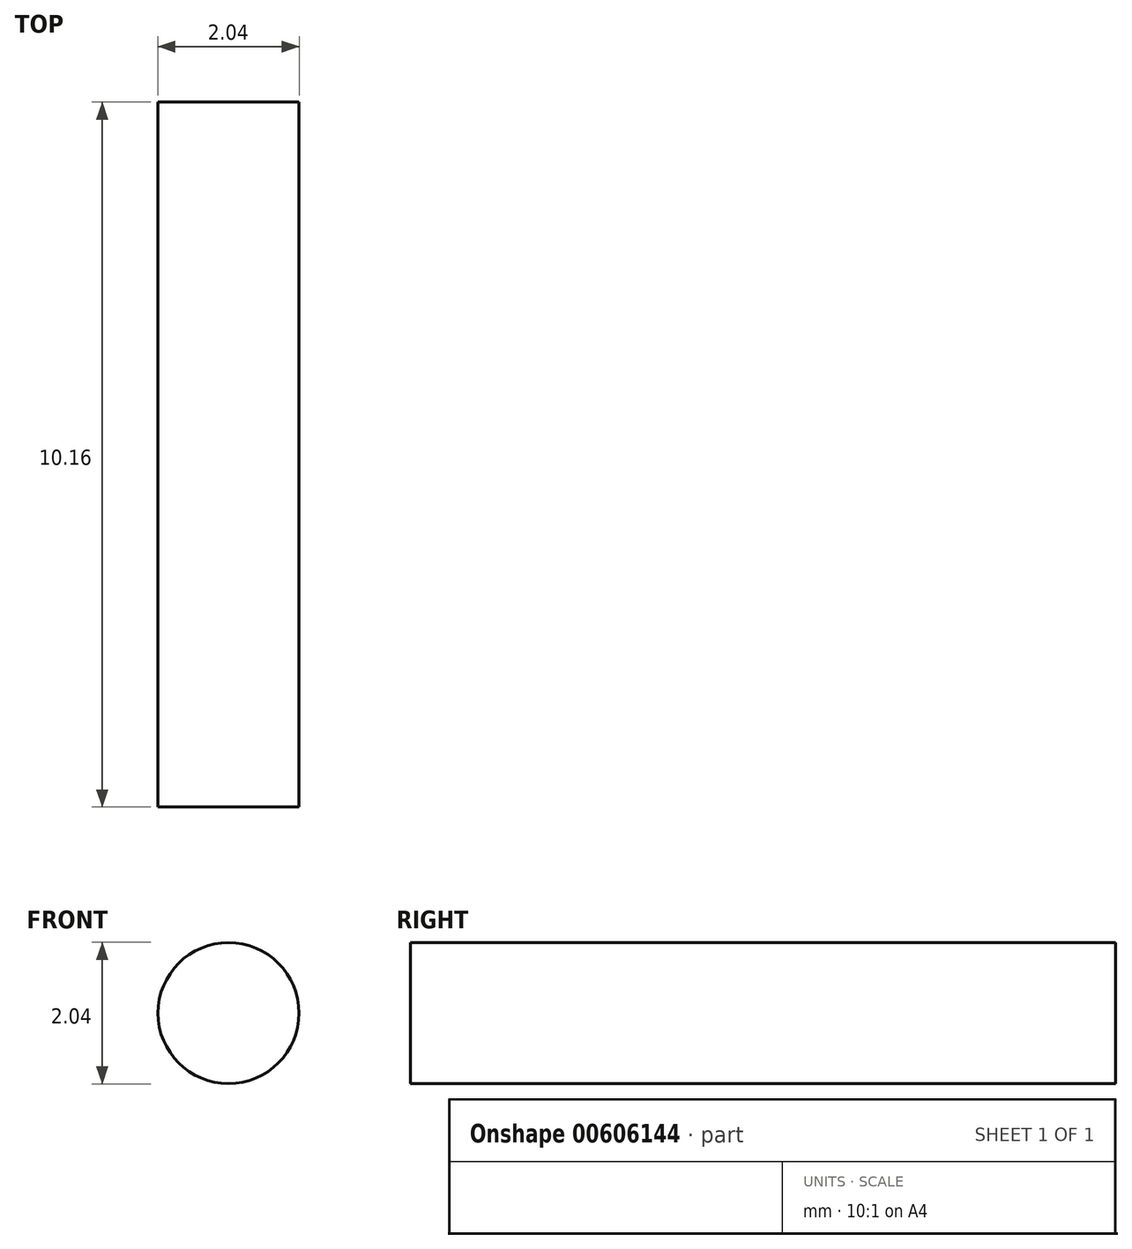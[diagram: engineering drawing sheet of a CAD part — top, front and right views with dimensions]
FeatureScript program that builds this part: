
annotation { "Feature Type Name" : "Feature", "Feature Type Description" : "" }
export const myFeature = defineFeature(function(context is Context, id is Id, definition is map)
    precondition{}
    {
        {
            var Q0;
            Q0=qCreatedBy(makeId("Front.planeOp"),FACE);
            var sketch = newSketch(context, id + "F0", { "sketchPlane" : qUnion([Q0])});
            skCircle(sketch, "E0", {"center": v(0, 0) * mm, "radius": 1.02 * mm});
            skSolve(sketch);
        }
        {
            var Q0;
            Q0 = qSketchRegion(id + "F0", true);
            var Q1;
            Q1=makeQuery(id+"F0.imprint","IMPRINT",FACE,{"disambiguationData":[TD([[makeQuery(id+"F0.imprint","IMPRINT",EDGE,{"derivedFrom":sQuery(id+"F0.wireOp",EDGE,"E0")}),1.0]])]});
            extrude(context, id + "F1", {"entities" : qUnion([Q0, Q1]), "depth" : 10.16 * mm, "offsetDistance" : 25.4 * mm});
        }
    });
